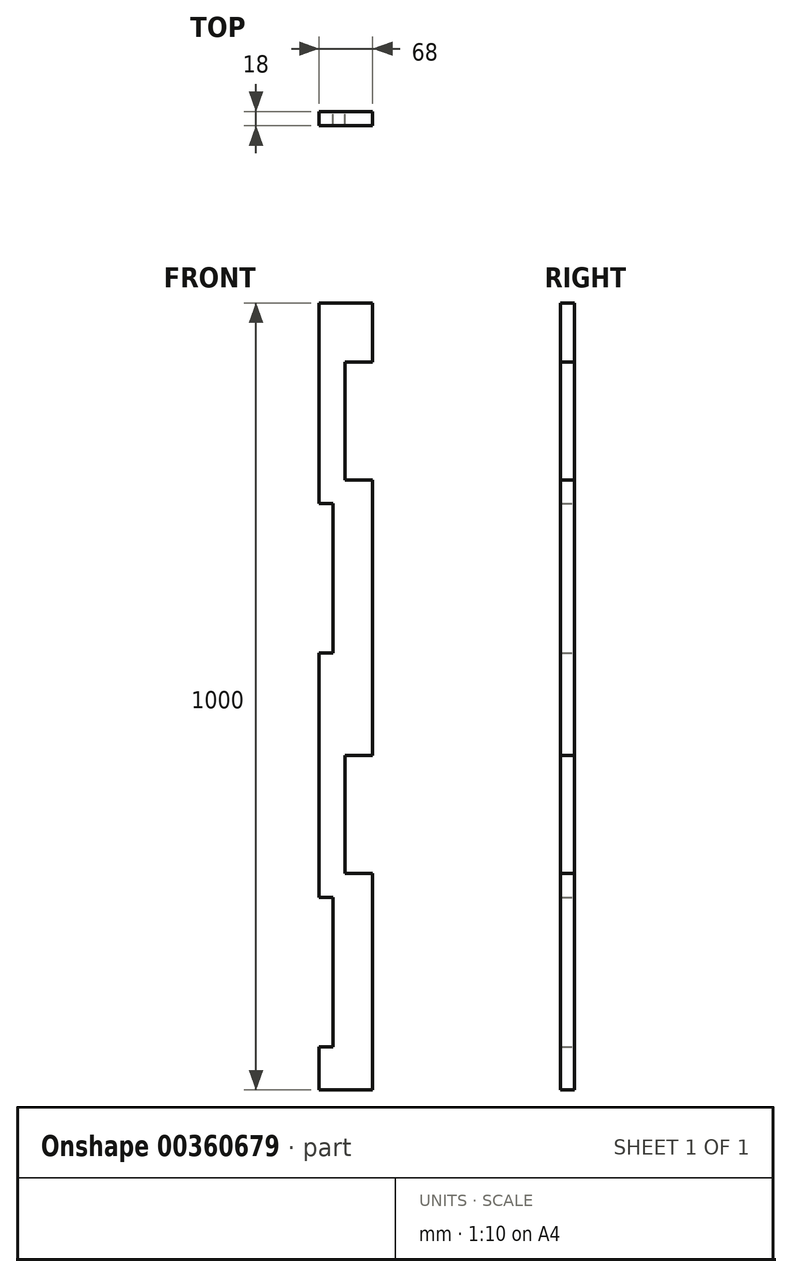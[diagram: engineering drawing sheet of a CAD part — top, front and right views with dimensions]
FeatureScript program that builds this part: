
annotation { "Feature Type Name" : "Feature", "Feature Type Description" : "" }
export const myFeature = defineFeature(function(context is Context, id is Id, definition is map)
    precondition{}
    {
        {
            var Q0;
            Q0=qCreatedBy(makeId("Front.planeOp"),FACE);
            var sketch = newSketch(context, id + "F0", { "sketchPlane" : qUnion([Q0])});
            skLineSegment(sketch, "E0.bottom", {"start": v(0, 0) * mm, "end": v(68, 0) * mm});
            skLineSegment(sketch, "E0.top", {"start": v(0, 1000) * mm, "end": v(68, 1000) * mm});
            skLineSegment(sketch, "E0.right", {"start": v(68, 0) * mm, "end": v(68, 275) * mm});
            skLineSegment(sketch, "E1.bottom", {"start": v(68, 275) * mm, "end": v(33, 275) * mm});
            skLineSegment(sketch, "E1.top", {"start": v(68, 425) * mm, "end": v(33, 425) * mm});
            skLineSegment(sketch, "E1.right", {"start": v(33, 275) * mm, "end": v(33, 425) * mm});
            skLineSegment(sketch, "E2.bottom", {"start": v(68, 925) * mm, "end": v(33, 925) * mm});
            skLineSegment(sketch, "E2.top", {"start": v(68, 775) * mm, "end": v(33, 775) * mm});
            skLineSegment(sketch, "E2.right", {"start": v(33, 925) * mm, "end": v(33, 775) * mm});
            skLineSegment(sketch, "E3.trimOffspring", {"start": v(68, 925) * mm, "end": v(68, 1000) * mm});
            skLineSegment(sketch, "E4.trimOffspring", {"start": v(68, 425) * mm, "end": v(68, 775) * mm});
            skLineSegment(sketch, "E5", {"start": v(0, 0) * mm, "end": v(0, 55) * mm});
            skLineSegment(sketch, "E6.bottom", {"start": v(0, 745) * mm, "end": v(18, 745) * mm});
            skLineSegment(sketch, "E6.top", {"start": v(0, 555) * mm, "end": v(18, 555) * mm});
            skLineSegment(sketch, "E6.right", {"start": v(18, 745) * mm, "end": v(18, 555) * mm});
            skLineSegment(sketch, "E7.bottom", {"start": v(0, 245) * mm, "end": v(18, 245) * mm});
            skLineSegment(sketch, "E7.top", {"start": v(0, 55) * mm, "end": v(18, 55) * mm});
            skLineSegment(sketch, "E7.right", {"start": v(18, 245) * mm, "end": v(18, 55) * mm});
            skLineSegment(sketch, "E8.trimOffspring", {"start": v(0, 745) * mm, "end": v(0, 1000) * mm});
            skLineSegment(sketch, "E9.trimOffspring", {"start": v(0, 245) * mm, "end": v(0, 555) * mm});
            skSolve(sketch);
        }
        {
            var Q0;
            Q0=makeQuery(id+"F0.imprint","IMPRINT",FACE,{"disambiguationData":[TD([[makeQuery(id+"F0.imprint","IMPRINT",EDGE,{"derivedFrom":sQuery(id+"F0.wireOp",EDGE,"E0.bottom")}),1.0]])]});
            extrude(context, id + "F1", {"entities" : qUnion([Q0]), "depth" : 18 * mm});
        }
    });
